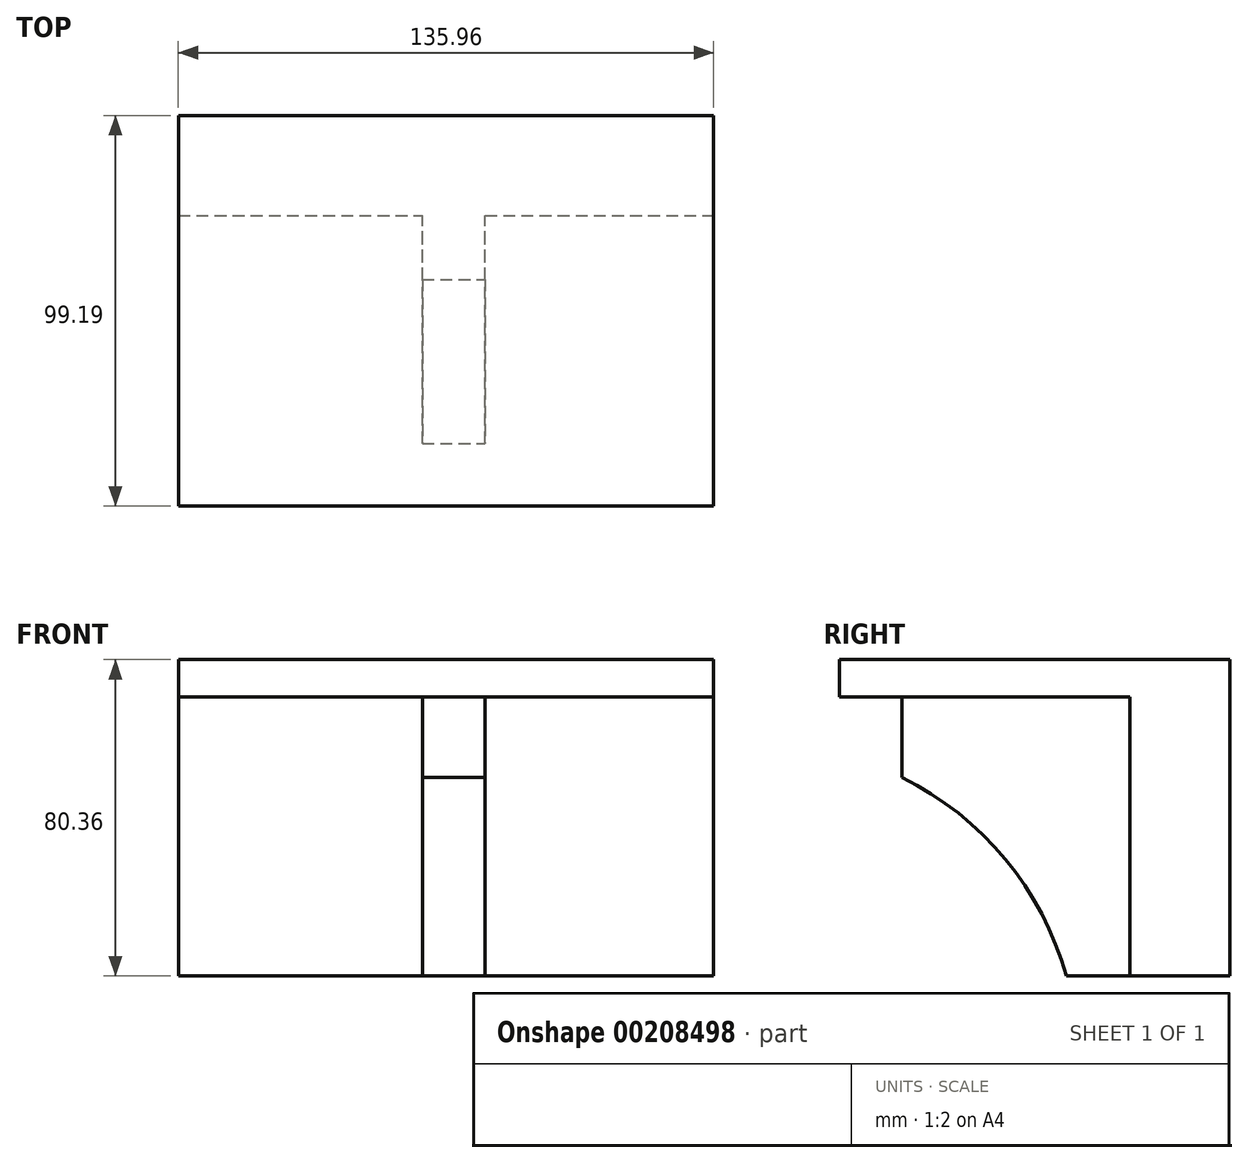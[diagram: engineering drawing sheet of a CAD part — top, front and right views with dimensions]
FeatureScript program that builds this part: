
annotation { "Feature Type Name" : "Feature", "Feature Type Description" : "" }
export const myFeature = defineFeature(function(context is Context, id is Id, definition is map)
    precondition{}
    {
        {
            var Q0;
            Q0=qCreatedBy(makeId("Front.planeOp"),FACE);
            var sketch = newSketch(context, id + "F0", { "sketchPlane" : qUnion([Q0])});
            skLineSegment(sketch, "E0.bottom", {"start": v(-51.98, 33.33) * mm, "end": v(83.98, 33.33) * mm});
            skLineSegment(sketch, "E0.top", {"start": v(-51.98, -37.5) * mm, "end": v(83.98, -37.5) * mm});
            skLineSegment(sketch, "E0.left", {"start": v(-51.98, 33.33) * mm, "end": v(-51.98, -37.5) * mm});
            skLineSegment(sketch, "E0.right", {"start": v(83.98, 33.33) * mm, "end": v(83.98, -37.5) * mm});
            skSolve(sketch);
        }
        {
            var Q0;
            Q0=makeQuery(id+"F0.imprint","IMPRINT",FACE,{"disambiguationData":[TD([[makeQuery(id+"F0.imprint","IMPRINT",EDGE,{"derivedFrom":sQuery(id+"F0.wireOp",EDGE,"E0.bottom")}),-1.0]])]});
            extrude(context, id + "F1", {"entities" : qUnion([Q0]), "depth" : 25.4 * mm});
        }
        {
            var Q0;
            Q0=makeQuery(id+"F1.opExtrude","SWEPT_FACE",FACE,{"disambiguationData":[OSD([sQuery(id+"F0.wireOp",EDGE,"E0.bottom")])]});
            var sketch = newSketch(context, id + "F2", { "sketchPlane" : qUnion([Q0])});
            skLineSegment(sketch, "E1.bottom", {"start": v(-51.98, 0) * mm, "end": v(83.98, 0) * mm});
            skLineSegment(sketch, "E1.top", {"start": v(-51.98, -99.2) * mm, "end": v(83.98, -99.2) * mm});
            skLineSegment(sketch, "E1.left", {"start": v(-51.98, 0) * mm, "end": v(-51.98, -99.2) * mm});
            skLineSegment(sketch, "E1.right", {"start": v(83.98, 0) * mm, "end": v(83.98, -99.2) * mm});
            skSolve(sketch);
        }
        {
            var Q0;
            {var subQ0=sQuery(id+"F2.wireOp",EDGE,"E1.top");Q0=makeQuery(id+"F2.imprint","IMPRINT",FACE,{"disambiguationData":[TD([[makeQuery(id+"F2.imprint","IMPRINT",EDGE,{"derivedFrom":subQ0}),1.0]])]});}
            var Q1;
            {var subQ0=sQuery(id+"F2.wireOp",EDGE,"E1.bottom");Q1=makeQuery(id+"F2.imprint","IMPRINT",FACE,{"disambiguationData":[TD([[makeQuery(id+"F2.imprint","IMPRINT",EDGE,{"derivedFrom":subQ0}),-1.0]])]});}
            extrude(context, id + "F3", {"entities" : qUnion([Q0, Q1]), "operationType" : NewBodyOperationType.ADD, "depth" : 9.52 * mm});
        }
        {
            var Q0;
            Q0=makeQuery(id+"F1.opExtrude","CAP_FACE",FACE,{"disambiguationData":[OSD([sQuery(id+"F0.wireOp",EDGE,"E0.bottom"),sQuery(id+"F0.wireOp",EDGE,"E0.top"),sQuery(id+"F0.wireOp",EDGE,"E0.left"),sQuery(id+"F0.wireOp",EDGE,"E0.right")])],"isStart":false});
            var sketch = newSketch(context, id + "F4", { "sketchPlane" : qUnion([Q0])});
            skLineSegment(sketch, "E2.bottom", {"start": v(10.02, 33.33) * mm, "end": v(26, 33.33) * mm});
            skLineSegment(sketch, "E2.top", {"start": v(10.02, -37.5) * mm, "end": v(26, -37.5) * mm});
            skLineSegment(sketch, "E2.left", {"start": v(10.02, 33.33) * mm, "end": v(10.02, -37.5) * mm});
            skLineSegment(sketch, "E2.right", {"start": v(26, 33.33) * mm, "end": v(26, -37.5) * mm});
            skSolve(sketch);
        }
        {
            var Q0;
            Q0=makeQuery(id+"F4.imprint","IMPRINT",FACE,{"disambiguationData":[TD([[makeQuery(id+"F4.imprint","IMPRINT",EDGE,{"derivedFrom":sQuery(id+"F4.wireOp",EDGE,"E2.bottom")}),-1.0]])]});
            extrude(context, id + "F5", {"entities" : qUnion([Q0]), "operationType" : NewBodyOperationType.ADD, "depth" : 57.9 * mm});
        }
        {
            var Q0;
            Q0=makeQuery(id+"F5.opExtrude","SWEPT_FACE",FACE,{"disambiguationData":[OSD([sQuery(id+"F4.wireOp",EDGE,"E2.right")])]});
            var sketch = newSketch(context, id + "F6", { "sketchPlane" : qUnion([Q0])});
            skCircle(sketch, "E3", {"center": v(-118.8, -58.98) * mm, "radius": 80.14 * mm});
            skSolve(sketch);
        }
        {
            var Q0;
            {var subQ0=sQuery(id+"F6.wireOp",EDGE,"E3");var subQ1=sQuery(id+"F4.wireOp",EDGE,"E2.right");var subQ4=makeQuery(id+"F5.opExtrude","CAP_EDGE",EDGE,{"disambiguationData":[OSD([subQ1])],"isStart":false});var subQ5=makeQuery(id+"F6.imprint","INTERSECT",VERTEX,{"derivedFrom":[subQ4,subQ0]});Q0=makeQuery(id+"F6.imprint","IMPRINT",FACE,{"disambiguationData":[TD([[makeQuery(id+"F6.imprint","IMPRINT",EDGE,{"disambiguationData":[TD([[subQ5,1.0]])],"derivedFrom":subQ0}),1.0]])]});}
            extrude(context, id + "F7", {"entities" : qUnion([Q0]), "operationType" : NewBodyOperationType.REMOVE, "oppositeDirection" : true, "depth" : 25.4 * mm});
        }
    });
